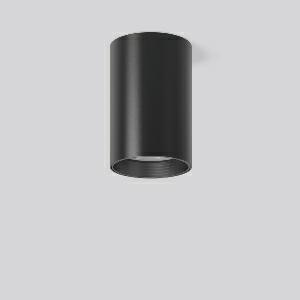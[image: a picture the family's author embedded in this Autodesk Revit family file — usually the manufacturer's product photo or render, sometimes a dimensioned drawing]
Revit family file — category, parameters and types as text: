
# Revit family: heledon_maxi_a_931221_003_1_76_6b5e
name_source: partatom
category: Lighting Fixtures
units: mm (PartAtom-declared; Revit-internal decimal feet)

## family parameters
Cut with Voids When Loaded = No
Host = Face
Light Source = No
Part Type = Normal
Room Calculation Point = No
Round Connector Dimension = Use Diameter
Shared = No

## types (1)
- HELEDON maxi A (1 x LED Modul 940, 2850 lm, 4000)
    Apparent Load = 25 VA
    Approval mark = CE
    CIE Flux Codes = 96 100 100 100 100
    Color Rendering = 92
    Color Temperature = 4000
    Default Elevation = 1800 mm
    Description = Series: HELEDON maxi
Cylindrical surface-mounted downlight. Housing: die-cast aluminium, powder-coated. Internal ceiling frame polycarbonate with bayonet mounting. Black plastic ring and recessed LED to prevent glare from the side. Optical assembly with lens made of plastic (polycarbonate) for the best homogeneous light distribution - can be changed without tools. Best colour rendering index Ra>90. Suitable for Ceiling mounting. Easy installation with a separate ceiling frame with bayonet mounting and plug connection. Driver integrated. Connected via plug-in connector. High quality converter without flickering and stroboscopic effect. The following accessories can be mounted without use of tools: interchangeable lenses, decorative glasses, honeycomb louvre, clear and frosted diffusers, white interchangeable plastic ring. 
Colour: deep black, matt (RAL 9005)
Diameter: 123 mm
Height: 183 mm
Lamp: LED
Socket: without socket
Colour temperature: 4000K
Colour rendering index (CRI): 92
System power: 25 W
Rated luminous flux: 2850 lm
Luminous efficiency: 114 lm/W
Control gear: Converter, dimmable, DALI
Protection class: I
Type of protection: IP 20
    Height = 183 mm
    Lamp = 1 x LED Modul 940
    Lamp Light Flux = 2850 lm
    Lamp count = 1
    Length = 123 mm
    Lifetime = 50000 h
    Luminous efficacy = 114 lm/W
    Manufacturer = RZB
    ModVariant = No
    Model = 931221.003.1.76
    Mounting Place = Ceiling
    Mounting Type = Surface mounted
    Number of Poles = 1
    OnlyDefault = Yes
    Power Factor = 1
    Product Name = HELEDON maxi A
    Product group = Surface mounted downlights
    ProductGroupID = 302
    Protection Class = Protection class I
    Protection Degree = IP 20
    RLX_Detail_Level = 1
    RLX_Emergency_Light_Flux = 0 lm
    RLX_Emergency_Type = 0
    RLX_Emergency_Type_DB = No
    RlxData = <blob elided: 96589 chars, md5=8e365767>
    Socket = socket
    Standby Power = 0 W
    System Light Flux = 2850 lm
    System Power = 25 W
    Type Comments = Product without accessories
    Type Image = 931193.003.jpg
    URL = http://relux.com
    VarID = ---
    Voltage = 230 V
    Voltage Range = 220-240 V
    Weight = 0.00 kg
    Width = 0 mm  [stored 0 ft]

note: [stored X ft] marks values corroborated as IEEE doubles in the binary element streams (Revit-internal decimal feet)

## geometry (parser evidence)
native form markers: Blend x4, Sweep x10
no freeform markers — native parametric forms only
